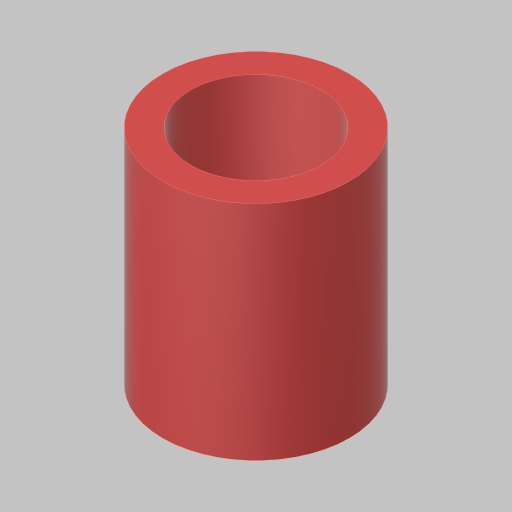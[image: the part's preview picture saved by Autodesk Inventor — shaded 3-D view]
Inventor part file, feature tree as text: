
AUTODESK INVENTOR PART (.ipt)
format: ipt  version: 2023.5 (Build 275446000, 446)  size: 104,448 bytes
history: native  units: in
note: dims shown in document units (in); Inventor stores cm internally (conversion verified against a paired STEP export)
features: extrude x1, sketch x1
ambient origin geometry x8: Origin, YZ Plane, XZ Plane, XY Plane, X Axis, Y Axis, Z Axis, Center Point
bodies: Solid1 (feature_tree)
feature tree (2):
  extrude  "Extrusion1"  Depth=0.99in
  sketch  "Sketch1"  dims[d0=0.58in d1=0.125in d2=0.99in d3=0.0in]
